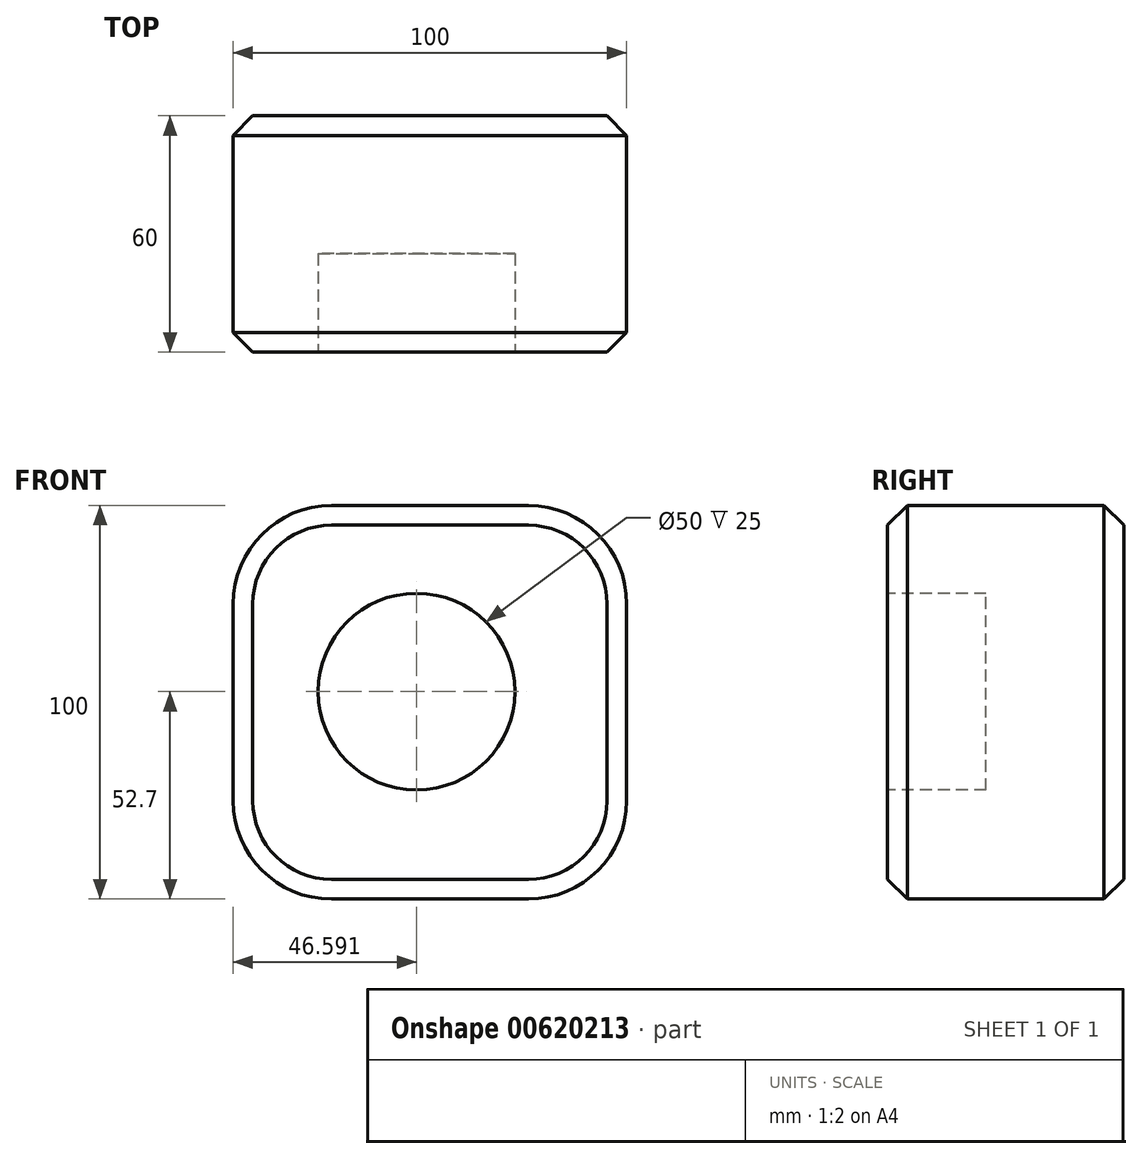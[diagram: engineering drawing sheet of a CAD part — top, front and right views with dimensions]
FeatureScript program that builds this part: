
annotation { "Feature Type Name" : "Feature", "Feature Type Description" : "" }
export const myFeature = defineFeature(function(context is Context, id is Id, definition is map)
    precondition{}
    {
        {
            var Q0;
            Q0=qCreatedBy(makeId("Front.planeOp"),FACE);
            var sketch = newSketch(context, id + "F0", { "sketchPlane" : qUnion([Q0])});
            skLineSegment(sketch, "E0.bottom", {"start": v(-16.57, 87.83) * mm, "end": v(33.43, 87.83) * mm});
            skLineSegment(sketch, "E0.top", {"start": v(-16.57, -12.17) * mm, "end": v(33.43, -12.17) * mm});
            skLineSegment(sketch, "E0.left", {"start": v(-41.57, 62.83) * mm, "end": v(-41.57, 12.83) * mm});
            skLineSegment(sketch, "E0.right", {"start": v(58.43, 62.83) * mm, "end": v(58.43, 12.83) * mm});
            skPoint(sketch, "E1.visualSharp", {"position": v(-41.57, 87.83) * mm});
            skArc(sketch, "E1.filletArc", {"start": v(-16.57, 87.83) * mm, "mid": v(-34.25, 80.5) * mm, "end": v(-41.57, 62.83) * mm});
            skPoint(sketch, "E2.visualSharp", {"position": v(58.43, -12.17) * mm});
            skArc(sketch, "E2.filletArc", {"start": v(33.43, -12.17) * mm, "mid": v(51.1, -4.85) * mm, "end": v(58.43, 12.83) * mm});
            skPoint(sketch, "E3.visualSharp", {"position": v(58.43, 87.83) * mm});
            skArc(sketch, "E3.filletArc", {"start": v(58.43, 62.83) * mm, "mid": v(51.1, 80.5) * mm, "end": v(33.43, 87.83) * mm});
            skPoint(sketch, "E4.visualSharp", {"position": v(-41.57, -12.17) * mm});
            skArc(sketch, "E4.filletArc", {"start": v(-41.57, 12.83) * mm, "mid": v(-34.25, -4.85) * mm, "end": v(-16.57, -12.17) * mm});
            skSolve(sketch);
        }
        {
            var Q0;
            Q0 = qSketchRegion(id + "F0", true);
            extrude(context, id + "F1", {"entities" : qUnion([Q0]), "depth" : 60 * mm, "offsetDistance" : 25 * mm});
        }
        {
            var Q0;
            Q0=makeQuery(id+"F1.opExtrude","CAP_FACE",FACE,{"disambiguationData":[OSD([sQuery(id+"F0.wireOp",EDGE,"E0.bottom"),sQuery(id+"F0.wireOp",EDGE,"E0.top"),sQuery(id+"F0.wireOp",EDGE,"E0.left"),sQuery(id+"F0.wireOp",EDGE,"E0.right"),sQuery(id+"F0.wireOp",EDGE,"E1.filletArc"),sQuery(id+"F0.wireOp",EDGE,"E2.filletArc"),sQuery(id+"F0.wireOp",EDGE,"E3.filletArc"),sQuery(id+"F0.wireOp",EDGE,"E4.filletArc")])],"isStart":false});
            var Q1;
            Q1=makeQuery(id+"F1.opExtrude","CAP_FACE",FACE,{"disambiguationData":[OSD([sQuery(id+"F0.wireOp",EDGE,"E0.bottom"),sQuery(id+"F0.wireOp",EDGE,"E0.top"),sQuery(id+"F0.wireOp",EDGE,"E0.left"),sQuery(id+"F0.wireOp",EDGE,"E0.right"),sQuery(id+"F0.wireOp",EDGE,"E1.filletArc"),sQuery(id+"F0.wireOp",EDGE,"E2.filletArc"),sQuery(id+"F0.wireOp",EDGE,"E3.filletArc"),sQuery(id+"F0.wireOp",EDGE,"E4.filletArc")])],"isStart":true});
            chamfer(context, id + "F2", {"entities" : qUnion([Q0, Q1]), "width" : 5 * mm, "tangentPropagation" : true});
        }
        {
            var Q0;
            Q0=makeQuery(id+"F1.opExtrude","CAP_FACE",FACE,{"disambiguationData":[OSD([sQuery(id+"F0.wireOp",EDGE,"E0.bottom"),sQuery(id+"F0.wireOp",EDGE,"E0.top"),sQuery(id+"F0.wireOp",EDGE,"E0.left"),sQuery(id+"F0.wireOp",EDGE,"E0.right"),sQuery(id+"F0.wireOp",EDGE,"E1.filletArc"),sQuery(id+"F0.wireOp",EDGE,"E2.filletArc"),sQuery(id+"F0.wireOp",EDGE,"E3.filletArc"),sQuery(id+"F0.wireOp",EDGE,"E4.filletArc")])],"isStart":false});
            var sketch = newSketch(context, id + "F3", { "sketchPlane" : qUnion([Q0])});
            skCircle(sketch, "E5", {"center": v(5.02, 40.53) * mm, "radius": 25 * mm});
            skSolve(sketch);
        }
        {
            var Q0;
            Q0 = qSketchRegion(id + "F3", true);
            extrude(context, id + "F4", {"entities" : qUnion([Q0]), "operationType" : NewBodyOperationType.REMOVE, "oppositeDirection" : true, "depth" : 25 * mm, "offsetDistance" : 25 * mm});
        }
    });
